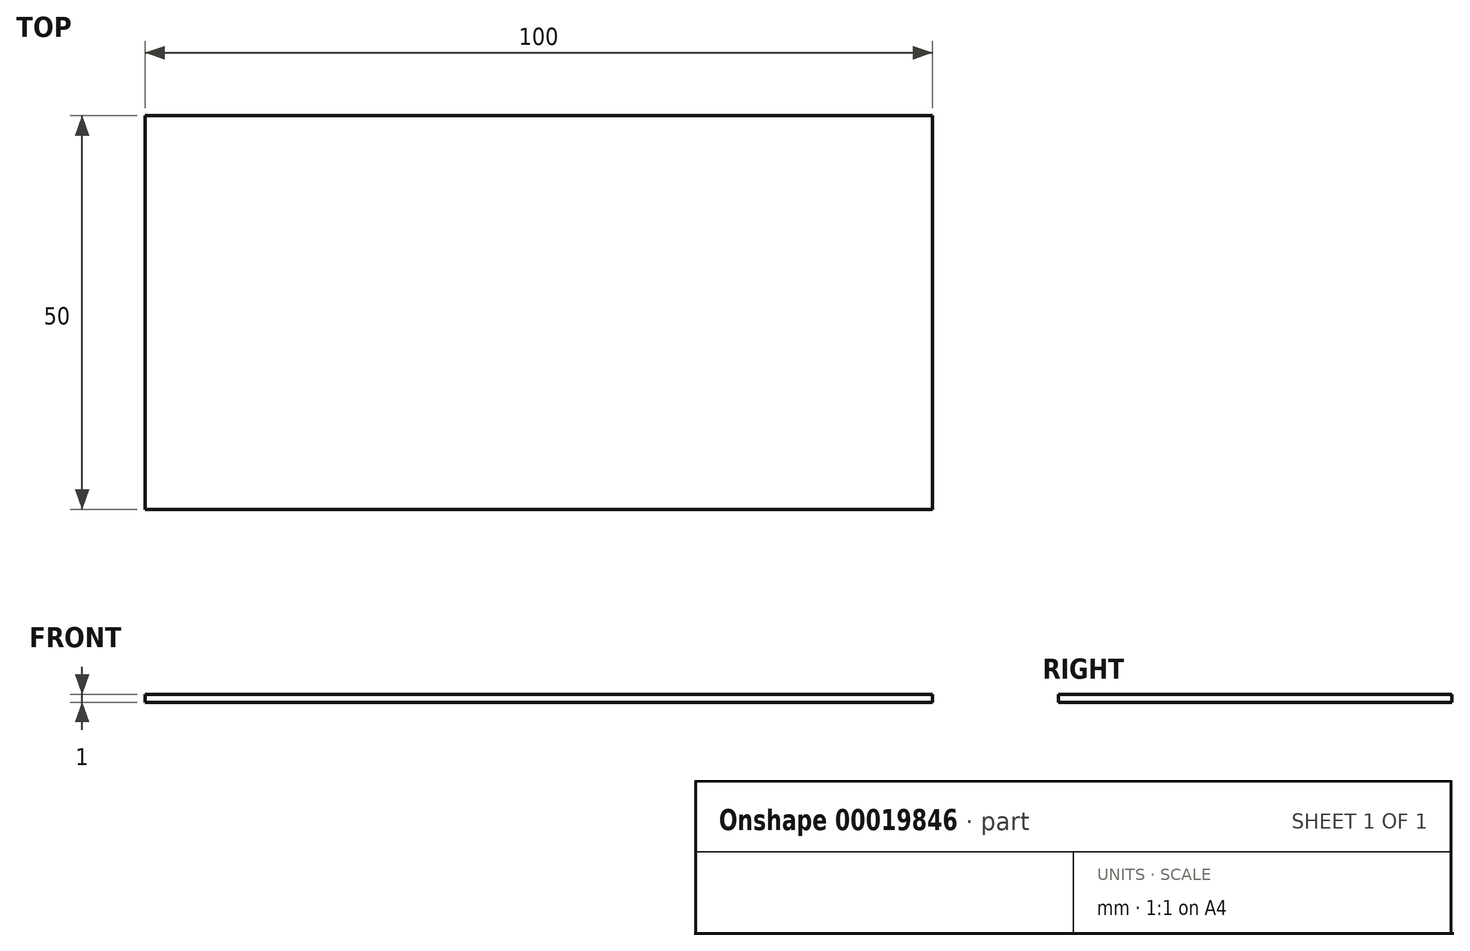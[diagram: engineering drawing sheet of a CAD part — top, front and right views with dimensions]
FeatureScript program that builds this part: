
annotation { "Feature Type Name" : "Feature", "Feature Type Description" : "" }
export const myFeature = defineFeature(function(context is Context, id is Id, definition is map)
    precondition{}
    {
        {
            var Q0;
            Q0=qCreatedBy(makeId("Top.planeOp"),FACE);
            var sketch = newSketch(context, id + "F0", { "sketchPlane" : qUnion([Q0])});
            skLineSegment(sketch, "E0.bottom", {"start": v(-50, 25) * mm, "end": v(50, 25) * mm});
            skLineSegment(sketch, "E0.top", {"start": v(-50, -25) * mm, "end": v(50, -25) * mm});
            skLineSegment(sketch, "E0.left", {"start": v(-50, 25) * mm, "end": v(-50, -25) * mm});
            skLineSegment(sketch, "E0.right", {"start": v(50, 25) * mm, "end": v(50, -25) * mm});
            skLineSegment(sketch, "E1", {"start": v(0, 25) * mm, "end": v(0, 0) * mm, "construction": true});
            skLineSegment(sketch, "E2", {"start": v(0, 0) * mm, "end": v(50, 0) * mm, "construction": true});
            skSolve(sketch);
        }
        {
            var Q0;
            Q0=makeQuery(id+"F0.imprint","IMPRINT",FACE,{"disambiguationData":[TD([[makeQuery(id+"F0.imprint","IMPRINT",EDGE,{"derivedFrom":sQuery(id+"F0.wireOp",EDGE,"E0.bottom")}),-1.0]])]});
            extrude(context, id + "F1", {"entities" : qUnion([Q0]), "oppositeDirection" : true, "depth" : 1 * mm});
        }
    });
